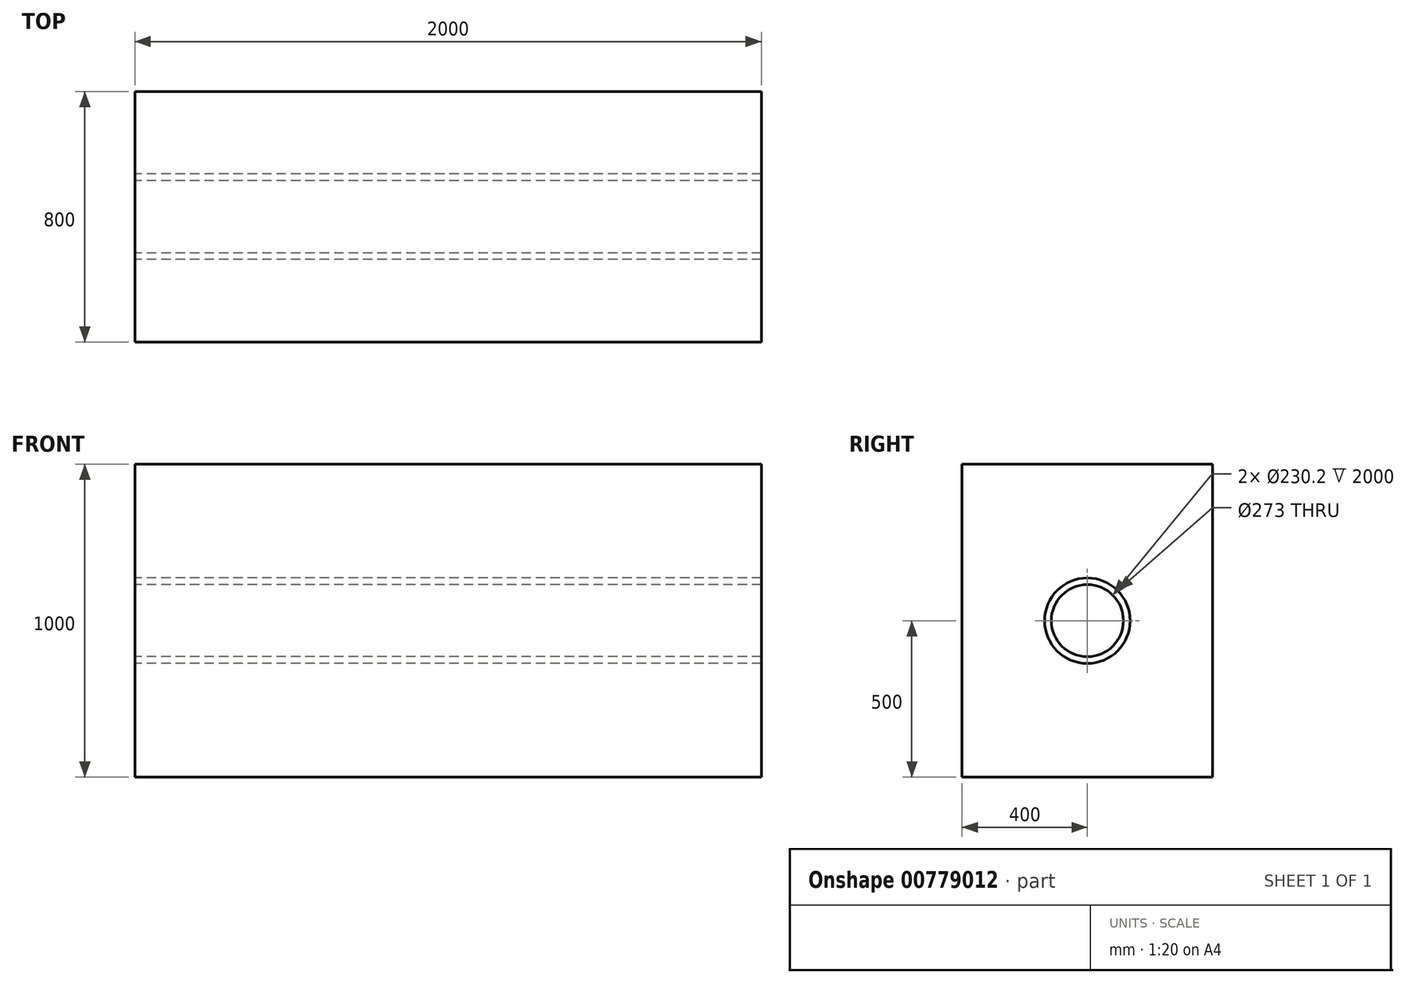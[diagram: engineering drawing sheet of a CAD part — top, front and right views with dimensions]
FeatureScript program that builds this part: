
annotation { "Feature Type Name" : "Feature", "Feature Type Description" : "" }
export const myFeature = defineFeature(function(context is Context, id is Id, definition is map)
    precondition{}
    {
        {
            var Q0;
            Q0=qCreatedBy(makeId("Top.planeOp"),FACE);
            var sketch = newSketch(context, id + "F0", { "sketchPlane" : qUnion([Q0])});
            skLineSegment(sketch, "E0.top", {"start": v(0, 21.4) * mm, "end": v(-2000, 21.4) * mm});
            skLineSegment(sketch, "E1", {"start": v(0, 300) * mm, "end": v(0, 536.5) * mm});
            skLineSegment(sketch, "E2", {"start": v(0, 536.5) * mm, "end": v(-2000, 536.5) * mm});
            skLineSegment(sketch, "E3", {"start": v(-2000, 536.5) * mm, "end": v(-2000, -263.5) * mm});
            skLineSegment(sketch, "E4", {"start": v(-2000, -263.5) * mm, "end": v(0, -263.5) * mm});
            skLineSegment(sketch, "E5", {"start": v(0, -263.5) * mm, "end": v(0, 300) * mm});
            skLineSegment(sketch, "E6", {"start": v(-2000, 21.4) * mm, "end": v(-2000, 0) * mm});
            skLineSegment(sketch, "E7", {"start": v(0, 21.4) * mm, "end": v(0, 0) * mm});
            skLineSegment(sketch, "E8", {"start": v(0, 21.4) * mm, "end": v(0, 136.5) * mm});
            skLineSegment(sketch, "E9", {"start": v(-2000, 21.4) * mm, "end": v(-2000, 136.5) * mm});
            skLineSegment(sketch, "E10", {"start": v(-2000, 136.5) * mm, "end": v(0, 136.5) * mm});
            skLineSegment(sketch, "E11", {"start": v(-2000, 0) * mm, "end": v(0, 0) * mm});
            skSolve(sketch);
        }
        {
            var Q0;
            {var subQ0=sQuery(id+"F0.wireOp",EDGE,"E0.top");Q0=makeQuery(id+"F0.imprint","IMPRINT",FACE,{"disambiguationData":[TD([[makeQuery(id+"F0.imprint","IMPRINT",EDGE,{"derivedFrom":subQ0}),1.0]])]});}
            var Q1;
            {var subQ0=sQuery(id+"F0.wireOp",EDGE,"E0.top");Q1=makeQuery(id+"F0.imprint","IMPRINT",FACE,{"disambiguationData":[TD([[makeQuery(id+"F0.imprint","IMPRINT",EDGE,{"derivedFrom":subQ0}),1.0]])]});}
            var Q2;
            {var subQ0=sQuery(id+"F0.wireOp",EDGE,"E0.top");Q2=makeQuery(id+"F0.imprint","IMPRINT",FACE,{"disambiguationData":[TD([[makeQuery(id+"F0.imprint","IMPRINT",EDGE,{"derivedFrom":subQ0}),1.0]])]});}
            var Q3;
            {var subQ0=sQuery(id+"F0.wireOp",EDGE,"E0.top");Q3=makeQuery(id+"F0.imprint","IMPRINT",FACE,{"disambiguationData":[TD([[makeQuery(id+"F0.imprint","IMPRINT",EDGE,{"derivedFrom":subQ0}),-1.0]])]});}
            var Q4;
            {var subQ0=sQuery(id+"F0.wireOp",EDGE,"E0.top");Q4=makeQuery(id+"F0.imprint","IMPRINT",FACE,{"disambiguationData":[TD([[makeQuery(id+"F0.imprint","IMPRINT",EDGE,{"derivedFrom":subQ0}),-1.0]])]});}
            var Q5;
            {var subQ0=sQuery(id+"F0.wireOp",EDGE,"E0.top");Q5=makeQuery(id+"F0.imprint","IMPRINT",FACE,{"disambiguationData":[TD([[makeQuery(id+"F0.imprint","IMPRINT",EDGE,{"derivedFrom":subQ0}),-1.0]])]});}
            var Q6;
            Q6=sQuery(id+"F0.wireOp",EDGE,"E10");
            revolve(context, id + "F1", {"surfaceOperationType" : NewSurfaceOperationType.NEW, "entities" : qUnion([Q0, Q1, Q2, Q3, Q4, Q5]), "axis" : qUnion([Q6]), "revolveType" : RevolveType.FULL});
        }
        {
            var Q0;
            {var subQ1=sQuery(id+"F0.wireOp",EDGE,"E1");Q0=makeQuery(id+"F0.imprint","IMPRINT",FACE,{"disambiguationData":[TD([[makeQuery(id+"F0.imprint","IMPRINT",EDGE,{"derivedFrom":subQ1}),1.0]])]});}
            var Q1;
            {var subQ2=sQuery(id+"F0.wireOp",EDGE,"E4");Q1=makeQuery(id+"F0.imprint","IMPRINT",FACE,{"disambiguationData":[TD([[makeQuery(id+"F0.imprint","IMPRINT",EDGE,{"derivedFrom":subQ2}),1.0]])]});}
            var Q2;
            {var subQ0=sQuery(id+"F0.wireOp",EDGE,"E0.top");Q2=makeQuery(id+"F0.imprint","IMPRINT",FACE,{"disambiguationData":[TD([[makeQuery(id+"F0.imprint","IMPRINT",EDGE,{"derivedFrom":subQ0}),-1.0]])]});}
            var Q3;
            {var subQ0=sQuery(id+"F0.wireOp",EDGE,"E0.top");Q3=makeQuery(id+"F0.imprint","IMPRINT",FACE,{"disambiguationData":[TD([[makeQuery(id+"F0.imprint","IMPRINT",EDGE,{"derivedFrom":subQ0}),1.0]])]});}
            extrude(context, id + "F2", {"entities" : qUnion([Q0, Q1, Q2, Q3]), "endBound" : BoundingType.SYMMETRIC, "depth" : 1000 * mm, "offsetDistance" : 25 * mm});
        }
        {
            var Q0;
            Q0=makeQuery(id+"F1.opRevolve","SWEPT_BODY",BODY,{"disambiguationData":[OSD([sQuery(id+"F0.wireOp",EDGE,"E3"),sQuery(id+"F0.wireOp",EDGE,"E5"),sQuery(id+"F0.wireOp",EDGE,"E10"),sQuery(id+"F0.wireOp",EDGE,"E11")])]});
            var Q1;
            Q1=makeQuery(id+"F2.opExtrude","SWEPT_BODY",BODY,{"disambiguationData":[OSD([sQuery(id+"F0.wireOp",EDGE,"E1"),sQuery(id+"F0.wireOp",EDGE,"E2"),sQuery(id+"F0.wireOp",EDGE,"E3"),sQuery(id+"F0.wireOp",EDGE,"E4"),sQuery(id+"F0.wireOp",EDGE,"E5")])]});
            booleanBodies(context, id + "F3", {"operationType" : BooleanOperationType.SUBTRACTION, "tools" : qUnion([Q0]), "targets" : qUnion([Q1]), "keepTools" : true});
        }
        {
            var Q0;
            {var subQ0=sQuery(id+"F0.wireOp",EDGE,"E0.top");Q0=makeQuery(id+"F0.imprint","IMPRINT",FACE,{"disambiguationData":[TD([[makeQuery(id+"F0.imprint","IMPRINT",EDGE,{"derivedFrom":subQ0}),1.0]])]});}
            var Q1;
            {var subQ0=sQuery(id+"F0.wireOp",EDGE,"E0.top");Q1=makeQuery(id+"F0.imprint","IMPRINT",FACE,{"disambiguationData":[TD([[makeQuery(id+"F0.imprint","IMPRINT",EDGE,{"derivedFrom":subQ0}),1.0]])]});}
            var Q2;
            Q2=sQuery(id+"F0.wireOp",EDGE,"E10");
            revolve(context, id + "F4", {"surfaceOperationType" : NewSurfaceOperationType.NEW, "entities" : qUnion([Q0, Q1]), "axis" : qUnion([Q2]), "revolveType" : RevolveType.FULL});
        }
        {
            var Q0;
            {var subQ0=sQuery(id+"F0.wireOp",EDGE,"E0.top");Q0=makeQuery(id+"F0.imprint","IMPRINT",FACE,{"disambiguationData":[TD([[makeQuery(id+"F0.imprint","IMPRINT",EDGE,{"derivedFrom":subQ0}),1.0]])]});}
            var Q1;
            Q1=sQuery(id+"F0.wireOp",EDGE,"E10");
            revolve(context, id + "F5", {"surfaceOperationType" : NewSurfaceOperationType.NEW, "entities" : qUnion([Q0]), "axis" : qUnion([Q1]), "revolveType" : RevolveType.FULL});
        }
    });
